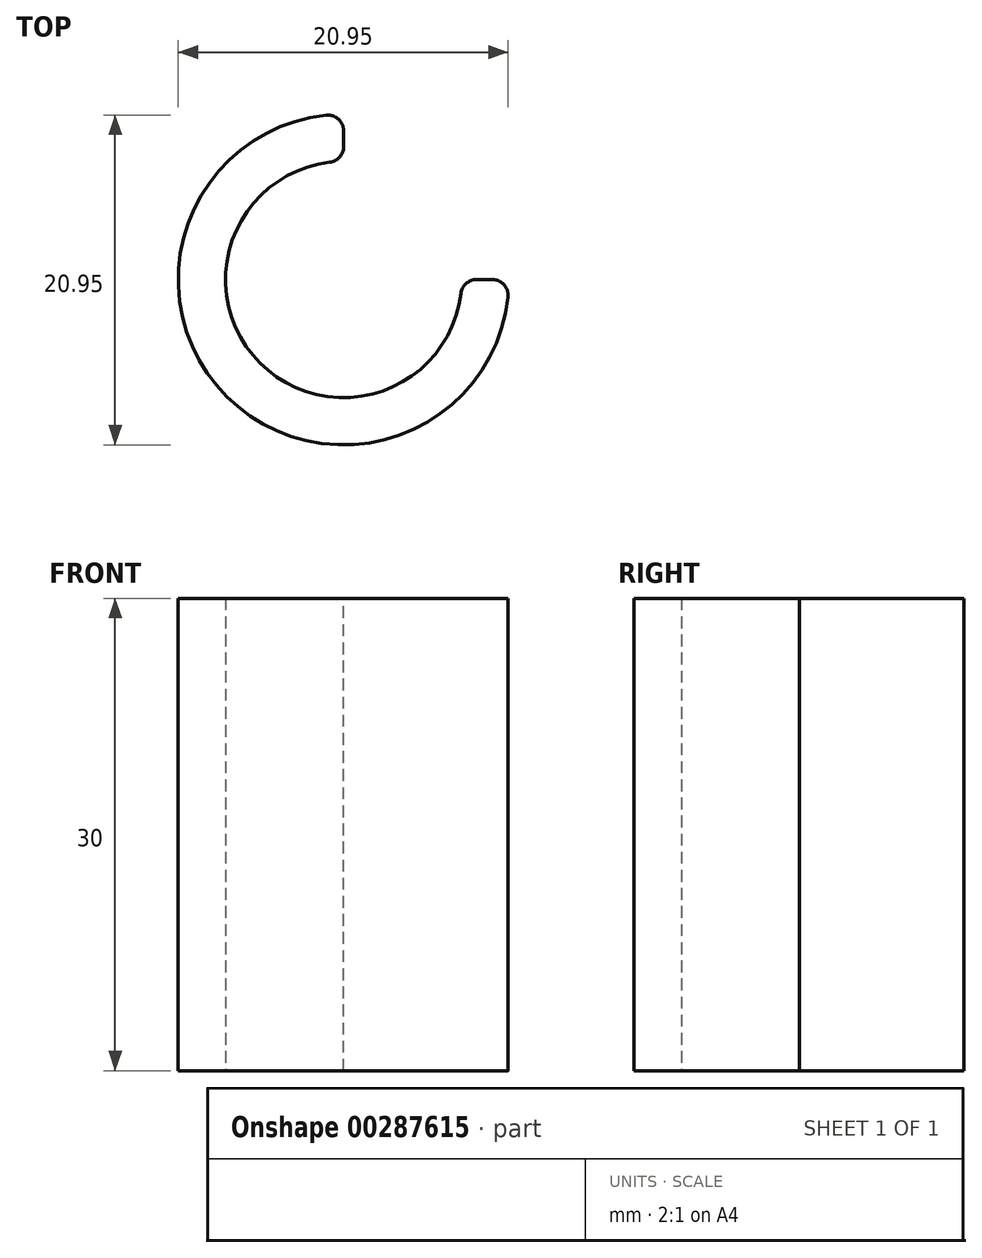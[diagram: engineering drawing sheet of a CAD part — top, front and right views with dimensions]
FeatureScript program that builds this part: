
annotation { "Feature Type Name" : "Feature", "Feature Type Description" : "" }
export const myFeature = defineFeature(function(context is Context, id is Id, definition is map)
    precondition{}
    {
        {
            var Q0;
            Q0=qCreatedBy(makeId("Top.planeOp"),FACE);
            var sketch = newSketch(context, id + "F0", { "sketchPlane" : qUnion([Q0])});
            skCircle(sketch, "E0", {"center": v(0, 0) * mm, "radius": 7.5 * mm});
            skCircle(sketch, "E1", {"center": v(0, 0) * mm, "radius": 10.5 * mm});
            skLineSegment(sketch, "E2", {"start": v(0, 0) * mm, "end": v(0, 10.5) * mm, "construction": true});
            skLineSegment(sketch, "E3", {"start": v(0, 0) * mm, "end": v(10.5, 0) * mm, "construction": true});
            skLineSegment(sketch, "E4", {"start": v(0, 10.5) * mm, "end": v(0, 7.5) * mm});
            skLineSegment(sketch, "E5", {"start": v(10.5, 0) * mm, "end": v(7.5, 0) * mm});
            skSolve(sketch);
        }
        {
            var Q0;
            {var subQ0=sQuery(id+"F0.wireOp",EDGE,"E4");Q0=makeQuery(id+"F0.imprint","IMPRINT",FACE,{"disambiguationData":[TD([[makeQuery(id+"F0.imprint","IMPRINT",EDGE,{"derivedFrom":subQ0}),-1.0]])]});}
            extrude(context, id + "F1", {"entities" : qUnion([Q0]), "depth" : 30 * mm});
        }
        {
            var Q0;
            Q0=makeQuery(id+"F1.opExtrude","SWEPT_EDGE",EDGE,{"disambiguationData":[OSD([sQuery(id+"F0.wireOp",EDGE,"E0"),sQuery(id+"F0.wireOp",EDGE,"E4")])]});
            var Q1;
            Q1=makeQuery(id+"F1.opExtrude","SWEPT_EDGE",EDGE,{"disambiguationData":[OSD([sQuery(id+"F0.wireOp",EDGE,"E1"),sQuery(id+"F0.wireOp",EDGE,"E4")])]});
            var Q2;
            Q2=makeQuery(id+"F1.opExtrude","SWEPT_EDGE",EDGE,{"disambiguationData":[OSD([sQuery(id+"F0.wireOp",EDGE,"E0"),sQuery(id+"F0.wireOp",EDGE,"E5")])]});
            var Q3;
            Q3=makeQuery(id+"F1.opExtrude","SWEPT_EDGE",EDGE,{"disambiguationData":[OSD([sQuery(id+"F0.wireOp",EDGE,"E1"),sQuery(id+"F0.wireOp",EDGE,"E5")])]});
            fillet(context, id + "F2", {"entities" : qUnion([Q0, Q1, Q2, Q3]), "radius" : 1 * mm, "tangentPropagation" : true, "allowEdgeOverflow" : false});
        }
    });
